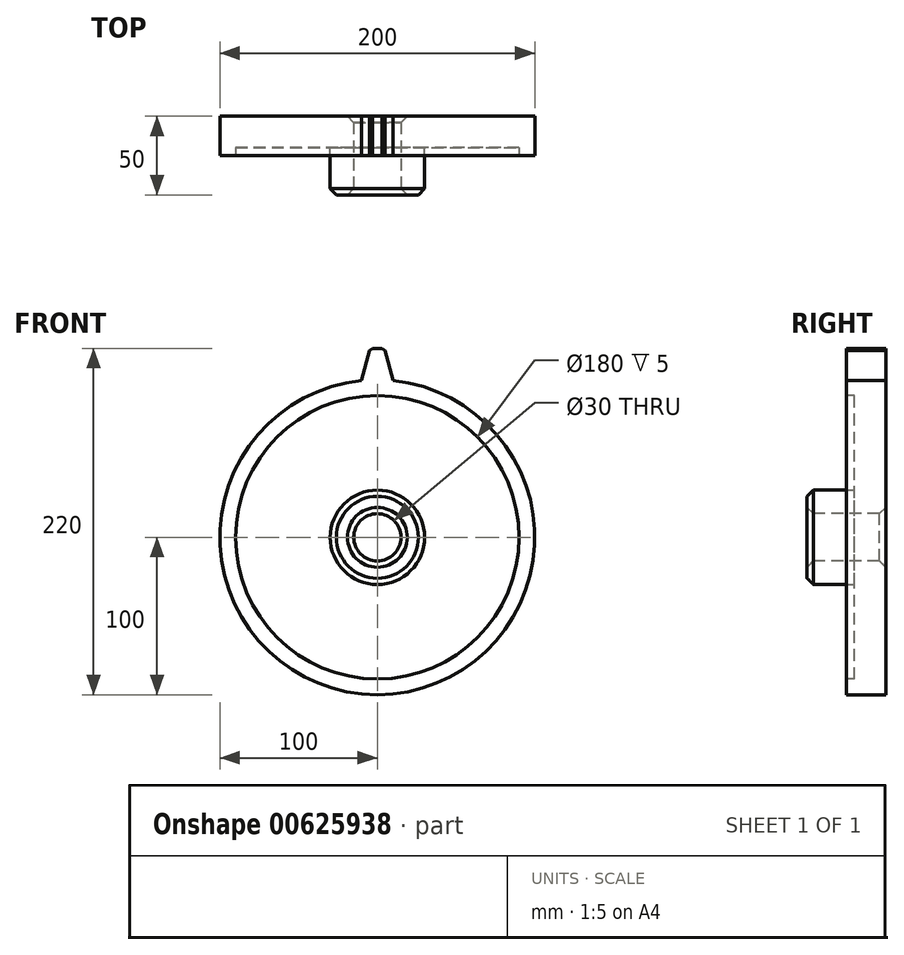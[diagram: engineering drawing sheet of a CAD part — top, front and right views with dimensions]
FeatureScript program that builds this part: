
annotation { "Feature Type Name" : "Feature", "Feature Type Description" : "" }
export const myFeature = defineFeature(function(context is Context, id is Id, definition is map)
    precondition{}
    {
        {
            var Q0;
            Q0=qCreatedBy(makeId("Front.planeOp"),FACE);
            var sketch = newSketch(context, id + "F0", { "sketchPlane" : qUnion([Q0])});
            skCircle(sketch, "E0", {"center": v(0, 0) * mm, "radius": 100 * mm});
            skSolve(sketch);
        }
        {
            var Q0;
            Q0 = qSketchRegion(id + "F0", true);
            extrude(context, id + "F1", {"entities" : qUnion([Q0]), "depth" : 25 * mm, "offsetDistance" : 25 * mm});
        }
        {
            var Q0;
            Q0=makeQuery(id+"F1.opExtrude","CAP_FACE",FACE,{"disambiguationData":[OSD([sQuery(id+"F0.wireOp",EDGE,"E0")])],"isStart":false});
            var sketch = newSketch(context, id + "F2", { "sketchPlane" : qUnion([Q0])});
            skCircle(sketch, "E1", {"center": v(0, 0) * mm, "radius": 120 * mm, "construction": true});
            skLineSegment(sketch, "E2", {"start": v(4.5, 120) * mm, "end": v(-4.5, 120) * mm});
            skPoint(sketch, "E3", {"position": v(0, 120) * mm});
            skLineSegment(sketch, "E4", {"start": v(-4.5, 120) * mm, "end": v(-10, 99.5) * mm});
            skLineSegment(sketch, "E5", {"start": v(4.5, 120) * mm, "end": v(10, 99.5) * mm});
            skLineSegment(sketch, "E6", {"start": v(-10, 99.5) * mm, "end": v(10, 99.5) * mm});
            skSolve(sketch);
        }
        {
            var Q0;
            {var subQ0=sQuery(id+"F2.wireOp",EDGE,"E6");Q0=makeQuery(id+"F2.imprint","IMPRINT",FACE,{"disambiguationData":[TD([[makeQuery(id+"F2.imprint","IMPRINT",EDGE,{"derivedFrom":subQ0}),-1.0]])]});}
            var Q1;
            Q1=makeQuery(id+"F2.imprint","IMPRINT",FACE,{"disambiguationData":[TD([[makeQuery(id+"F2.imprint","IMPRINT",EDGE,{"derivedFrom":sQuery(id+"F2.wireOp",EDGE,"E2")}),1.0]])]});
            extrude(context, id + "F3", {"entities" : qUnion([Q0, Q1]), "operationType" : NewBodyOperationType.ADD, "oppositeDirection" : true, "depth" : 25 * mm, "offsetDistance" : 25 * mm});
        }
        {
            var Q0;
            Q0=makeQuery(id+"F3.opExtrude","SWEPT_EDGE",EDGE,{"disambiguationData":[OSD([sQuery(id+"F2.wireOp",EDGE,"E2"),sQuery(id+"F2.wireOp",EDGE,"E4")])]});
            var Q1;
            Q1=makeQuery(id+"F3.opExtrude","SWEPT_EDGE",EDGE,{"disambiguationData":[OSD([sQuery(id+"F2.wireOp",EDGE,"E2"),sQuery(id+"F2.wireOp",EDGE,"E5")])]});
            chamfer(context, id + "F4", {"entities" : qUnion([Q0, Q1]), "width" : 2 * mm, "tangentPropagation" : true});
        }
        {
            var Q0;
            Q0=makeQuery(id+"F3.opExtrude","SWEPT_EDGE",EDGE,{"disambiguationData":[OSD([sQuery(id+"F0.wireOp",EDGE,"E0"),sQuery(id+"F2.wireOp",EDGE,"E5"),sQuery(id+"F2.wireOp",EDGE,"E6")]),OD(0.0)]});
            var Q1;
            Q1=makeQuery(id+"F3.opExtrude","SWEPT_EDGE",EDGE,{"disambiguationData":[OSD([sQuery(id+"F0.wireOp",EDGE,"E0"),sQuery(id+"F2.wireOp",EDGE,"E4"),sQuery(id+"F2.wireOp",EDGE,"E6")]),OD(0.0)]});
            fillet(context, id + "F5", {"entities" : qUnion([Q0, Q1]), "radius" : 5 * mm, "tangentPropagation" : true, "allowEdgeOverflow" : false});
        }
        {
            var Q0;
            {var subQ0=sQuery(id+"F2.wireOp",EDGE,"E5");var subQ1=sQuery(id+"F2.wireOp",EDGE,"E4");var subQ2=sQuery(id+"F2.wireOp",EDGE,"E2");var subQ3=sQuery(id+"F0.wireOp",EDGE,"E0");Q0=makeQuery(id+"FQcCe5ykcFTGAyO_1.19.F3.boolean.opBoolean","MERGE",FACE,{"derivedFrom":[makeQuery(id+"FQcCe5ykcFTGAyO_1.18.F3.boolean.opBoolean","MERGE",FACE,{"derivedFrom":[makeQuery(id+"FQcCe5ykcFTGAyO_1.17.F3.boolean.opBoolean","MERGE",FACE,{"derivedFrom":[makeQuery(id+"FQcCe5ykcFTGAyO_1.16.F3.boolean.opBoolean","MERGE",FACE,{"derivedFrom":[makeQuery(id+"FQcCe5ykcFTGAyO_1.15.F3.boolean.opBoolean","MERGE",FACE,{"derivedFrom":[makeQuery(id+"FQcCe5ykcFTGAyO_1.14.F3.boolean.opBoolean","MERGE",FACE,{"derivedFrom":[makeQuery(id+"FQcCe5ykcFTGAyO_1.13.F3.boolean.opBoolean","MERGE",FACE,{"derivedFrom":[makeQuery(id+"FQcCe5ykcFTGAyO_1.12.F3.boolean.opBoolean","MERGE",FACE,{"derivedFrom":[makeQuery(id+"FQcCe5ykcFTGAyO_1.11.F3.boolean.opBoolean","MERGE",FACE,{"derivedFrom":[makeQuery(id+"FQcCe5ykcFTGAyO_1.10.F3.boolean.opBoolean","MERGE",FACE,{"derivedFrom":[makeQuery(id+"FQcCe5ykcFTGAyO_1.9.F3.boolean.opBoolean","MERGE",FACE,{"derivedFrom":[makeQuery(id+"FQcCe5ykcFTGAyO_1.8.F3.boolean.opBoolean","MERGE",FACE,{"derivedFrom":[makeQuery(id+"FQcCe5ykcFTGAyO_1.7.F3.boolean.opBoolean","MERGE",FACE,{"derivedFrom":[makeQuery(id+"FQcCe5ykcFTGAyO_1.6.F3.boolean.opBoolean","MERGE",FACE,{"derivedFrom":[makeQuery(id+"FQcCe5ykcFTGAyO_1.5.F3.boolean.opBoolean","MERGE",FACE,{"derivedFrom":[makeQuery(id+"FQcCe5ykcFTGAyO_1.4.F3.boolean.opBoolean","MERGE",FACE,{"derivedFrom":[makeQuery(id+"FQcCe5ykcFTGAyO_1.3.F3.boolean.opBoolean","MERGE",FACE,{"derivedFrom":[makeQuery(id+"FQcCe5ykcFTGAyO_1.2.F3.boolean.opBoolean","MERGE",FACE,{"derivedFrom":[makeQuery(id+"FQcCe5ykcFTGAyO_1.1.F3.boolean.opBoolean","MERGE",FACE,{"derivedFrom":[makeQuery(id+"F3.boolean.opBoolean","MERGE",FACE,{"derivedFrom":[makeQuery(id+"F1.opExtrude","CAP_FACE",FACE,{"disambiguationData":[OSD([subQ3])],"isStart":false}),makeQuery(id+"F3.opExtrude","CAP_FACE",FACE,{"disambiguationData":[OSD([subQ3,subQ2,subQ1,subQ0])],"isStart":true})]}),makeQuery(id+"FQcCe5ykcFTGAyO_1.1.F3.opExtrude","CAP_FACE",FACE,{"disambiguationData":[OSD([subQ3,subQ2,subQ1,subQ0])],"isStart":true})]}),makeQuery(id+"FQcCe5ykcFTGAyO_1.2.F3.opExtrude","CAP_FACE",FACE,{"disambiguationData":[OSD([subQ3,subQ2,subQ1,subQ0])],"isStart":true})]}),makeQuery(id+"FQcCe5ykcFTGAyO_1.3.F3.opExtrude","CAP_FACE",FACE,{"disambiguationData":[OSD([subQ3,subQ2,subQ1,subQ0])],"isStart":true})]}),makeQuery(id+"FQcCe5ykcFTGAyO_1.4.F3.opExtrude","CAP_FACE",FACE,{"disambiguationData":[OSD([subQ3,subQ2,subQ1,subQ0])],"isStart":true})]}),makeQuery(id+"FQcCe5ykcFTGAyO_1.5.F3.opExtrude","CAP_FACE",FACE,{"disambiguationData":[OSD([subQ3,subQ2,subQ1,subQ0])],"isStart":true})]}),makeQuery(id+"FQcCe5ykcFTGAyO_1.6.F3.opExtrude","CAP_FACE",FACE,{"disambiguationData":[OSD([subQ3,subQ2,subQ1,subQ0])],"isStart":true})]}),makeQuery(id+"FQcCe5ykcFTGAyO_1.7.F3.opExtrude","CAP_FACE",FACE,{"disambiguationData":[OSD([subQ3,subQ2,subQ1,subQ0])],"isStart":true})]}),makeQuery(id+"FQcCe5ykcFTGAyO_1.8.F3.opExtrude","CAP_FACE",FACE,{"disambiguationData":[OSD([subQ3,subQ2,subQ1,subQ0])],"isStart":true})]}),makeQuery(id+"FQcCe5ykcFTGAyO_1.9.F3.opExtrude","CAP_FACE",FACE,{"disambiguationData":[OSD([subQ3,subQ2,subQ1,subQ0])],"isStart":true})]}),makeQuery(id+"FQcCe5ykcFTGAyO_1.10.F3.opExtrude","CAP_FACE",FACE,{"disambiguationData":[OSD([subQ3,subQ2,subQ1,subQ0])],"isStart":true})]}),makeQuery(id+"FQcCe5ykcFTGAyO_1.11.F3.opExtrude","CAP_FACE",FACE,{"disambiguationData":[OSD([subQ3,subQ2,subQ1,subQ0])],"isStart":true})]}),makeQuery(id+"FQcCe5ykcFTGAyO_1.12.F3.opExtrude","CAP_FACE",FACE,{"disambiguationData":[OSD([subQ3,subQ2,subQ1,subQ0])],"isStart":true})]}),makeQuery(id+"FQcCe5ykcFTGAyO_1.13.F3.opExtrude","CAP_FACE",FACE,{"disambiguationData":[OSD([subQ3,subQ2,subQ1,subQ0])],"isStart":true})]}),makeQuery(id+"FQcCe5ykcFTGAyO_1.14.F3.opExtrude","CAP_FACE",FACE,{"disambiguationData":[OSD([subQ3,subQ2,subQ1,subQ0])],"isStart":true})]}),makeQuery(id+"FQcCe5ykcFTGAyO_1.15.F3.opExtrude","CAP_FACE",FACE,{"disambiguationData":[OSD([subQ3,subQ2,subQ1,subQ0])],"isStart":true})]}),makeQuery(id+"FQcCe5ykcFTGAyO_1.16.F3.opExtrude","CAP_FACE",FACE,{"disambiguationData":[OSD([subQ3,subQ2,subQ1,subQ0])],"isStart":true})]}),makeQuery(id+"FQcCe5ykcFTGAyO_1.17.F3.opExtrude","CAP_FACE",FACE,{"disambiguationData":[OSD([subQ3,subQ2,subQ1,subQ0])],"isStart":true})]}),makeQuery(id+"FQcCe5ykcFTGAyO_1.18.F3.opExtrude","CAP_FACE",FACE,{"disambiguationData":[OSD([subQ3,subQ2,subQ1,subQ0])],"isStart":true})]}),makeQuery(id+"FQcCe5ykcFTGAyO_1.19.F3.opExtrude","CAP_FACE",FACE,{"disambiguationData":[OSD([subQ3,subQ2,subQ1,subQ0])],"isStart":true})]});}
            var sketch = newSketch(context, id + "F6", { "sketchPlane" : qUnion([Q0])});
            skCircle(sketch, "E7", {"center": v(0, 0) * mm, "radius": 90 * mm});
            skSolve(sketch);
        }
        {
            var Q0;
            Q0 = qSketchRegion(id + "F6", true);
            extrude(context, id + "F7", {"entities" : qUnion([Q0]), "operationType" : NewBodyOperationType.REMOVE, "oppositeDirection" : true, "depth" : 5 * mm, "offsetDistance" : 25 * mm});
        }
        {
            var Q0;
            Q0=makeQuery(id+"F7.boolean.opBoolean","COPY",FACE,{"derivedFrom":makeQuery(id+"F7.opExtrude","CAP_FACE",FACE,{"disambiguationData":[OSD([sQuery(id+"F6.wireOp",EDGE,"E7")])],"isStart":false})});
            var sketch = newSketch(context, id + "F8", { "sketchPlane" : qUnion([Q0])});
            skCircle(sketch, "E8", {"center": v(0, 0) * mm, "radius": 30 * mm});
            skSolve(sketch);
        }
        {
            var Q0;
            Q0 = qSketchRegion(id + "F8", true);
            extrude(context, id + "F9", {"entities" : qUnion([Q0]), "operationType" : NewBodyOperationType.ADD, "depth" : 30 * mm, "offsetDistance" : 25 * mm});
        }
        {
            var Q0;
            Q0=makeQuery(id+"F9.opExtrude","CAP_FACE",FACE,{"disambiguationData":[OSD([sQuery(id+"F8.wireOp",EDGE,"E8")])],"isStart":false});
            var sketch = newSketch(context, id + "F10", { "sketchPlane" : qUnion([Q0])});
            skCircle(sketch, "E9", {"center": v(0, 0) * mm, "radius": 15 * mm});
            skSolve(sketch);
        }
        {
            var Q0;
            Q0 = qSketchRegion(id + "F10", true);
            extrude(context, id + "F11", {"entities" : qUnion([Q0]), "operationType" : NewBodyOperationType.REMOVE, "endBound" : BoundingType.THROUGH_ALL, "oppositeDirection" : true, "depth" : 25 * mm, "offsetDistance" : 25 * mm});
        }
        {
            var Q0;
            Q0=makeQuery(id+"F11.boolean.opBoolean","COPY",FACE,{"derivedFrom":makeQuery(id+"F11.opExtrude","SWEPT_FACE",FACE,{"disambiguationData":[OSD([sQuery(id+"F10.wireOp",EDGE,"E9")])]})});
            var Q1;
            Q1=makeQuery(id+"F9.opExtrude","CAP_FACE",FACE,{"disambiguationData":[OSD([sQuery(id+"F8.wireOp",EDGE,"E8")])],"isStart":false});
            chamfer(context, id + "F12", {"entities" : qUnion([Q0, Q1]), "width" : 4 * mm, "tangentPropagation" : true});
        }
    });
